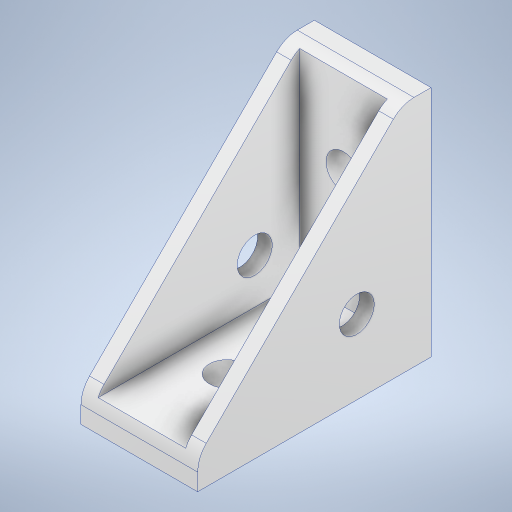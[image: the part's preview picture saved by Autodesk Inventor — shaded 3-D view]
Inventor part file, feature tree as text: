
AUTODESK INVENTOR PART (.ipt)
format: ipt  version: 2024.3 (Build 283343000, 343)  size: 323,072 bytes
history: native  units: mm
features: sketch x7, extrude x5, hole x2, other x1, fillet x1
ambient origin geometry x8: Origin, YZ Plane, XZ Plane, XY Plane, X Axis, Y Axis, Z Axis, Center Point
bodies: Body1 (feature_tree), Body2 (feature_tree), Body3 (feature_tree)
feature tree (16):
  other  "ソリッド1"
  extrude  "押し出し1"  Depth=20.0mm
  extrude  "押し出し2"  Depth=40.0mm
  extrude  "押し出し3"  Depth=40.0mm TaperAngle=0.0deg
  extrude  "押し出し4"  Depth=5.0mm
  extrude  "押し出し5"  Depth=5.0mm
  hole  "穴1"  [1 undecoded]
  hole  "穴2"  [1 undecoded]
  fillet  "フィレット1"  Radius=2.5mm
  sketch  "スケッチ1"
  sketch  "スケッチ2"
  sketch  "スケッチ4"
  sketch  "スケッチ5"
  sketch  "スケッチ6"
  sketch  "スケッチ7"
  sketch  "スケッチ8"
note: 2 required parameter values undecoded (feature->parameter linkage not recoverable at this tier; creation-order binding heuristic only, values carry confidence <= 0.55)
